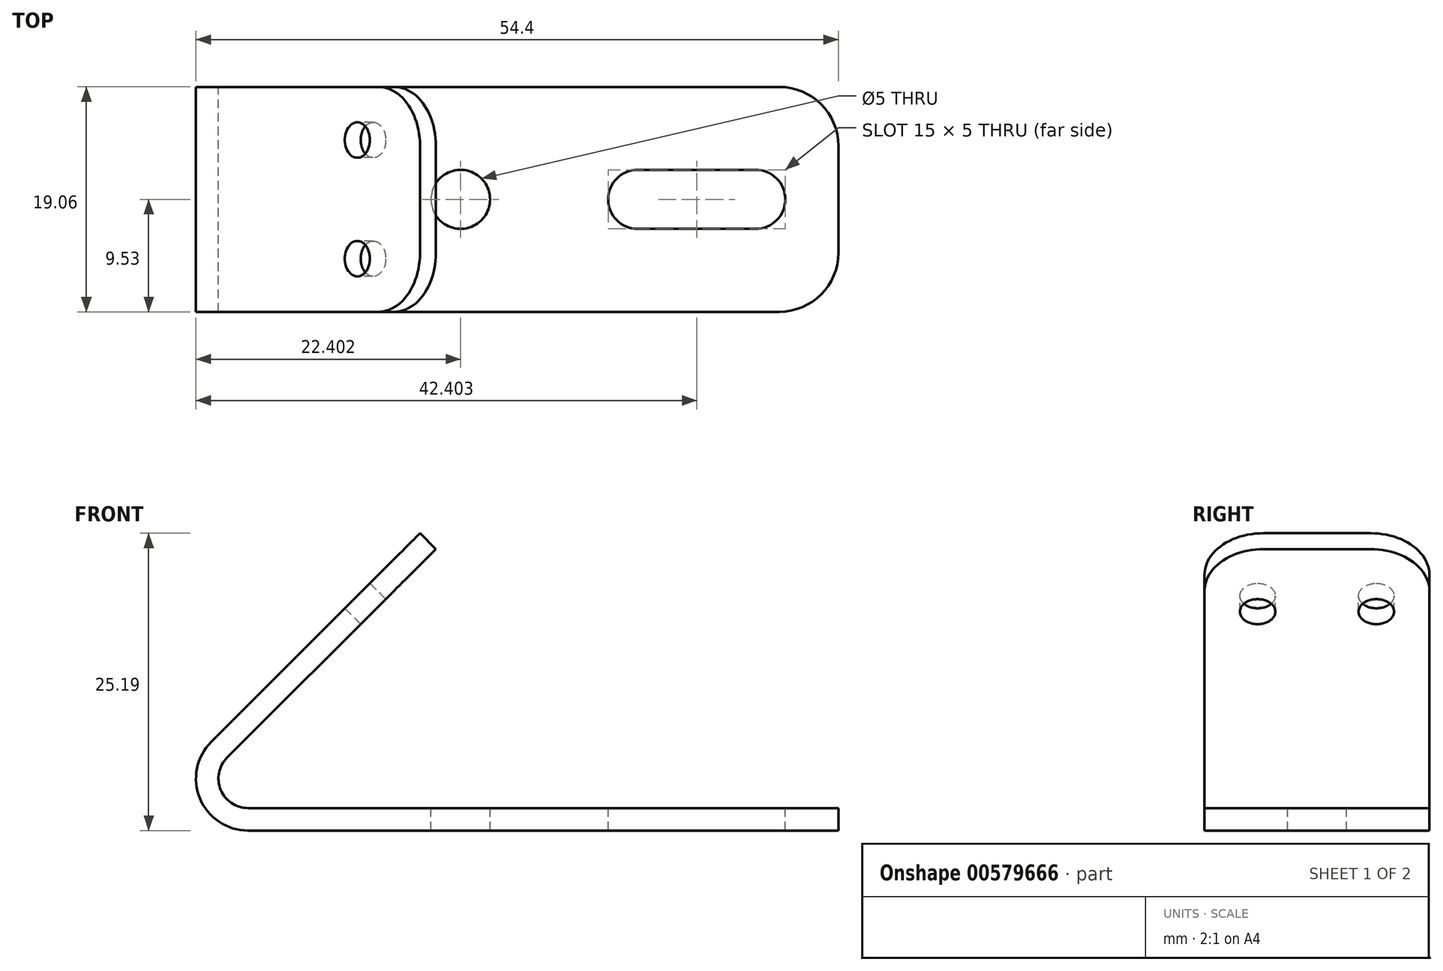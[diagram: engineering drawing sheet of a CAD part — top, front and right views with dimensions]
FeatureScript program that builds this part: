
annotation { "Feature Type Name" : "Feature", "Feature Type Description" : "" }
export const myFeature = defineFeature(function(context is Context, id is Id, definition is map)
    precondition{}
    {
        {
            var Q0;
            Q0=qCreatedBy(makeId("Front.planeOp"),FACE);
            var sketch = newSketch(context, id + "F0", { "sketchPlane" : qUnion([Q0])});
            skLineSegment(sketch, "E0", {"start": v(10.62, 0) * mm, "end": v(60.62, 0) * mm});
            skLineSegment(sketch, "E1", {"start": v(60.62, 0) * mm, "end": v(60.62, 1.9) * mm});
            skLineSegment(sketch, "E2", {"start": v(60.62, 1.9) * mm, "end": v(0, 1.9) * mm});
            skLineSegment(sketch, "E3", {"start": v(7.51, 7.51) * mm, "end": v(25.19, 25.19) * mm});
            skPoint(sketch, "E4.visualSharp", {"position": v(0, 0) * mm});
            skArc(sketch, "E4.filletArc", {"start": v(7.51, 7.51) * mm, "mid": v(6.56, 2.72) * mm, "end": v(10.62, 0) * mm});
            skLineSegment(sketch, "E5", {"start": v(25.19, 25.19) * mm, "end": v(26.53, 23.85) * mm});
            skLineSegment(sketch, "E6", {"start": v(26.53, 23.85) * mm, "end": v(8.85, 6.17) * mm});
            skArc(sketch, "E7", {"start": v(8.85, 6.17) * mm, "mid": v(8.31, 3.44) * mm, "end": v(10.62, 1.9) * mm});
            skSolve(sketch);
        }
        {
            var Q0;
            Q0=qSketchRegion(id+"F0",true);
            extrude(context, id + "F1", {"entities" : qUnion([Q0]), "endBound" : BoundingType.SYMMETRIC, "depth" : 19.05 * mm, "offsetDistance" : 25 * mm});
        }
        {
            var Q0;
            Q0=makeQuery(id+"F1.opExtrude","SWEPT_FACE",FACE,{"disambiguationData":[OSD([sQuery(id+"F0.wireOp",EDGE,"E2")])]});
            var sketch = newSketch(context, id + "F2", { "sketchPlane" : qUnion([Q0])});
            skLineSegment(sketch, "E8.0", {"start": v(60.62, -9.53) * mm, "end": v(60.62, 9.52) * mm});
            skLineSegment(sketch, "E9.0", {"start": v(60.62, 9.53) * mm, "end": v(10.62, 9.53) * mm});
            skLineSegment(sketch, "E10.0", {"start": v(60.62, -9.53) * mm, "end": v(10.62, -9.53) * mm});
            skLineSegment(sketch, "E11", {"start": v(60.62, 0) * mm, "end": v(56.12, 0) * mm});
            skLineSegment(sketch, "E12", {"start": v(56.12, 0) * mm, "end": v(41.12, 0) * mm});
            skLineSegment(sketch, "E13", {"start": v(56.12, 0) * mm, "end": v(56.12, 2.5) * mm});
            skCircle(sketch, "E14", {"center": v(53.62, 0) * mm, "radius": 2.5 * mm});
            skCircle(sketch, "E15", {"center": v(43.62, 0) * mm, "radius": 2.5 * mm});
            skLineSegment(sketch, "E16", {"start": v(43.62, 2.5) * mm, "end": v(53.62, 2.5) * mm});
            skLineSegment(sketch, "E17", {"start": v(43.62, -2.5) * mm, "end": v(53.62, -2.5) * mm});
            skCircle(sketch, "E18", {"center": v(28.62, 0) * mm, "radius": 2.5 * mm});
            skSolve(sketch);
        }
        {
            var Q0;
            Q0=qSketchRegion(id+"F2",true);
            extrude(context, id + "F3", {"entities" : qUnion([Q0]), "operationType" : NewBodyOperationType.REMOVE, "endBound" : BoundingType.THROUGH_ALL, "oppositeDirection" : true, "depth" : 25 * mm, "offsetDistance" : 25 * mm});
        }
        {
            var Q0;
            Q0=makeQuery(id+"F1.opExtrude","SWEPT_FACE",FACE,{"disambiguationData":[OSD([sQuery(id+"F0.wireOp",EDGE,"E3")])]});
            var sketch = newSketch(context, id + "F4", { "sketchPlane" : qUnion([Q0])});
            skLineSegment(sketch, "E19.0", {"start": v(9.53, 35.62) * mm, "end": v(-9.52, 35.62) * mm});
            skLineSegment(sketch, "E19.1", {"start": v(9.53, 10.62) * mm, "end": v(-9.52, 10.62) * mm});
            skLineSegment(sketch, "E19.2", {"start": v(-9.53, 10.62) * mm, "end": v(-9.53, 35.62) * mm});
            skLineSegment(sketch, "E19.3", {"start": v(9.53, 10.62) * mm, "end": v(9.53, 35.62) * mm});
            skLineSegment(sketch, "E20", {"start": v(-9.53, 35.62) * mm, "end": v(-9.53, 28.12) * mm});
            skCircle(sketch, "E21", {"center": v(-5.03, 28.12) * mm, "radius": 1.5 * mm});
            skLineSegment(sketch, "E22", {"start": v(9.53, 6.22) * mm, "end": v(-9.52, 6.22) * mm});
            skCircle(sketch, "E23", {"center": v(5.03, 28.12) * mm, "radius": 1.5 * mm});
            skSolve(sketch);
        }
        {
            var Q0;
            Q0=makeQuery(id+"F4.imprint","IMPRINT",FACE,{"disambiguationData":[TD([[makeQuery(id+"F4.imprint","IMPRINT",EDGE,{"derivedFrom":sQuery(id+"F4.wireOp",EDGE,"E21")}),1.0]])]});
            var Q1;
            Q1=makeQuery(id+"F4.imprint","IMPRINT",FACE,{"disambiguationData":[TD([[makeQuery(id+"F4.imprint","IMPRINT",EDGE,{"derivedFrom":sQuery(id+"F4.wireOp",EDGE,"E23")}),1.0]])]});
            extrude(context, id + "F5", {"entities" : qUnion([Q0, Q1]), "operationType" : NewBodyOperationType.REMOVE, "endBound" : BoundingType.UP_TO_NEXT, "oppositeDirection" : true, "depth" : 25 * mm, "offsetDistance" : 25 * mm});
        }
        {
            var Q0;
            Q0=makeQuery(id+"F1.opExtrude","CAP_EDGE",EDGE,{"disambiguationData":[OSD([sQuery(id+"F0.wireOp",EDGE,"E5")])],"isStart":true});
            var Q1;
            Q1=makeQuery(id+"F1.opExtrude","CAP_EDGE",EDGE,{"disambiguationData":[OSD([sQuery(id+"F0.wireOp",EDGE,"E5")])],"isStart":false});
            var Q2;
            Q2=makeQuery(id+"F1.opExtrude","CAP_EDGE",EDGE,{"disambiguationData":[OSD([sQuery(id+"F0.wireOp",EDGE,"E1")])],"isStart":false});
            var Q3;
            Q3=makeQuery(id+"F1.opExtrude","CAP_EDGE",EDGE,{"disambiguationData":[OSD([sQuery(id+"F0.wireOp",EDGE,"E1")])],"isStart":true});
            fillet(context, id + "F6", {"entities" : qUnion([Q0, Q1, Q2, Q3]), "radius" : 5 * mm, "tangentPropagation" : true, "allowEdgeOverflow" : false});
        }
    });
